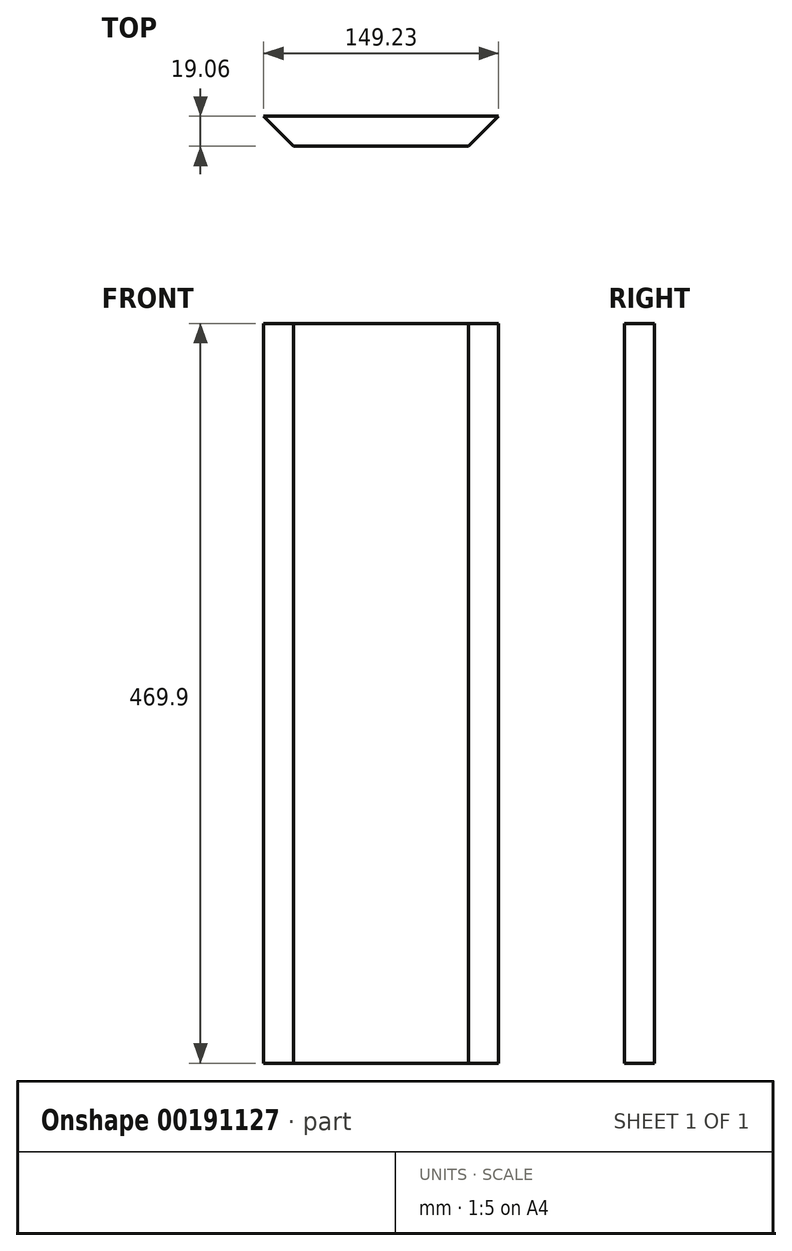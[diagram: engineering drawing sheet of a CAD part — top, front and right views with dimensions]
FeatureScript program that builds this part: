
annotation { "Feature Type Name" : "Feature", "Feature Type Description" : "" }
export const myFeature = defineFeature(function(context is Context, id is Id, definition is map)
    precondition{}
    {
        {
            var Q0;
            Q0=qCreatedBy(makeId("Top.planeOp"),FACE);
            var sketch = newSketch(context, id + "F0", { "sketchPlane" : qUnion([Q0])});
            skLineSegment(sketch, "E0.bottom", {"start": v(60.32, 9.52) * mm, "end": v(-88.9, 9.52) * mm});
            skLineSegment(sketch, "E0.top", {"start": v(41.27, -9.53) * mm, "end": v(-69.85, -9.53) * mm});
            skPoint(sketch, "E0.middle", {"position": v(0, 0) * mm});
            skLineSegment(sketch, "E1", {"start": v(-88.9, 9.52) * mm, "end": v(-69.85, -9.53) * mm});
            skLineSegment(sketch, "E2", {"start": v(60.32, 9.52) * mm, "end": v(41.27, -9.53) * mm});
            skPoint(sketch, "E0.right.end.orphan", {"position": v(-60.32, -9.53) * mm});
            skPoint(sketch, "E0.left.end.orphan", {"position": v(88.9, -9.52) * mm});
            skSolve(sketch);
        }
        {
            var Q0;
            Q0 = qSketchRegion(id + "F0", true);
            extrude(context, id + "F1", {"entities" : qUnion([Q0]), "depth" : 469.9 * mm});
        }
    });
